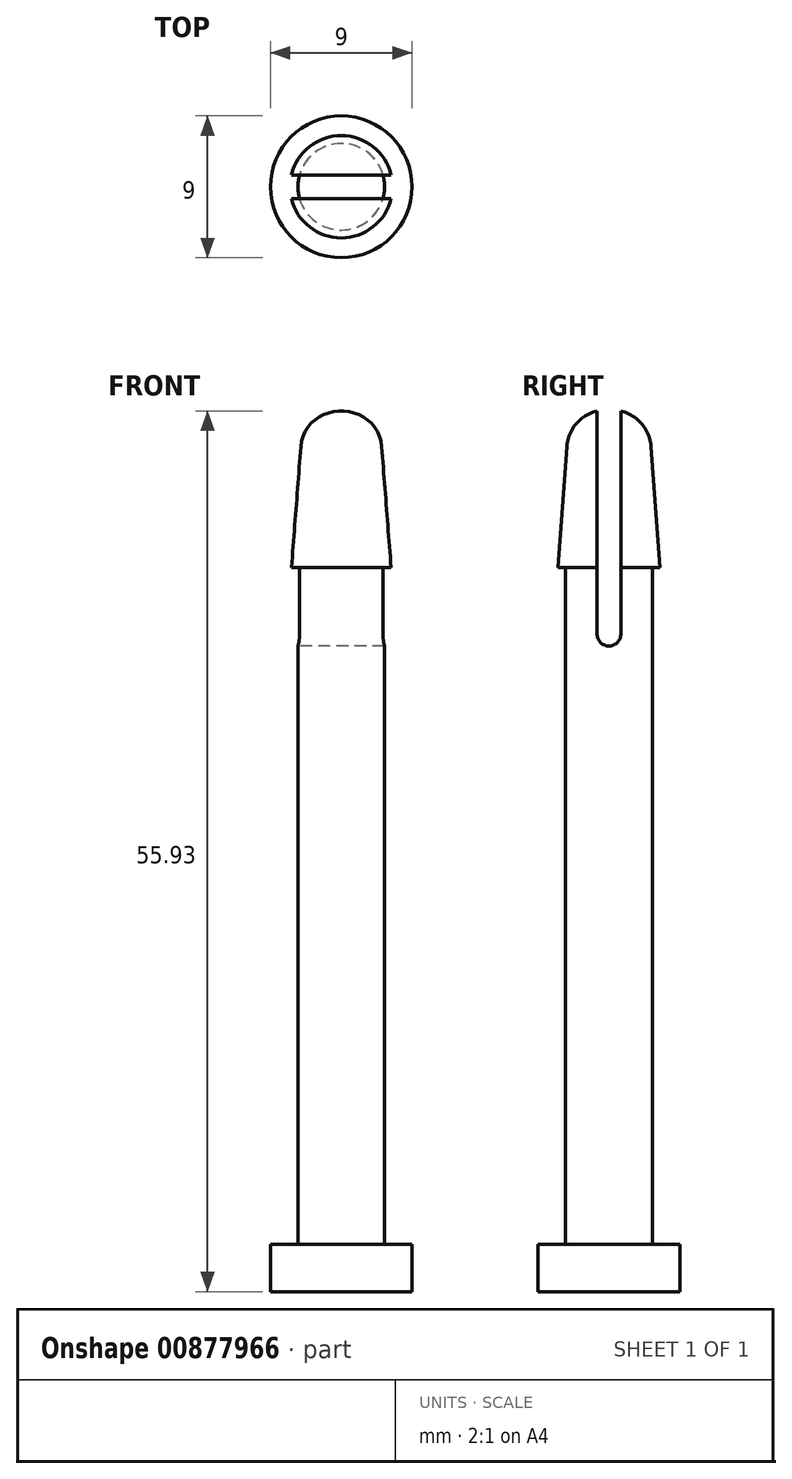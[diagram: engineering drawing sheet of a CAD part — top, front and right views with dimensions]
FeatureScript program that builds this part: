
annotation { "Feature Type Name" : "Feature", "Feature Type Description" : "" }
export const myFeature = defineFeature(function(context is Context, id is Id, definition is map)
    precondition{}
    {
        {
            var Q0;
            Q0=qCreatedBy(makeId("Top.planeOp"),FACE);
            var sketch = newSketch(context, id + "F0", { "sketchPlane" : qUnion([Q0])});
            skCircle(sketch, "E0", {"center": v(0, 0) * mm, "radius": 4.5 * mm});
            skSolve(sketch);
        }
        {
            var Q0;
            Q0 = qSketchRegion(id + "F0", true);
            extrude(context, id + "F1", {"entities" : qUnion([Q0]), "depth" : 3 * mm, "offsetDistance" : 25 * mm});
        }
        {
            var Q0;
            Q0=makeQuery(id+"F1.opExtrude","CAP_FACE",FACE,{"disambiguationData":[OSD([sQuery(id+"F0.wireOp",EDGE,"E0")])],"isStart":false});
            var sketch = newSketch(context, id + "F2", { "sketchPlane" : qUnion([Q0])});
            skCircle(sketch, "E1", {"center": v(0, 0) * mm, "radius": 2.75 * mm});
            skSolve(sketch);
        }
        {
            var Q0;
            Q0 = qSketchRegion(id + "F2", true);
            extrude(context, id + "F3", {"entities" : qUnion([Q0]), "operationType" : NewBodyOperationType.ADD, "depth" : 43 * mm, "offsetDistance" : 25 * mm});
        }
        {
            var Q0;
            Q0=qCreatedBy(makeId("Front.planeOp"),FACE);
            var sketch = newSketch(context, id + "F4", { "sketchPlane" : qUnion([Q0])});
            skLineSegment(sketch, "E2", {"start": v(0, 46) * mm, "end": v(3.25, 46) * mm});
            skLineSegment(sketch, "E3", {"start": v(3.25, 46) * mm, "end": v(2.5, 56) * mm});
            skLineSegment(sketch, "E4", {"start": v(2.5, 56) * mm, "end": v(0, 56) * mm});
            skLineSegment(sketch, "E5", {"start": v(0, 56) * mm, "end": v(0, 46) * mm});
            skSolve(sketch);
        }
        {
            var Q0;
            Q0 = qSketchRegion(id + "F4", true);
            var Q1;
            Q1=sQuery(id+"F4.wireOp",EDGE,"E5");
            revolve(context, id + "F5", {"operationType" : NewBodyOperationType.ADD, "surfaceOperationType" : NewSurfaceOperationType.NEW, "entities" : qUnion([Q0]), "axis" : qUnion([Q1]), "revolveType" : RevolveType.FULL});
        }
        {
            var Q0;
            Q0=makeQuery(id+"F5.opRevolve","SWEPT_FACE",FACE,{"disambiguationData":[OSD([sQuery(id+"F4.wireOp",EDGE,"E4")])]});
            var sketch = newSketch(context, id + "F6", { "sketchPlane" : qUnion([Q0])});
            skLineSegment(sketch, "E6.bottom", {"start": v(-5, 0.75) * mm, "end": v(5, 0.75) * mm});
            skLineSegment(sketch, "E6.top", {"start": v(-5, -0.75) * mm, "end": v(5, -0.75) * mm});
            skLineSegment(sketch, "E6.left", {"start": v(-5, 0.75) * mm, "end": v(-5, -0.75) * mm});
            skLineSegment(sketch, "E6.right", {"start": v(5, 0.75) * mm, "end": v(5, -0.75) * mm});
            skLineSegment(sketch, "E7", {"start": v(-5, -0.75) * mm, "end": v(5, 0.75) * mm, "construction": true});
            skLineSegment(sketch, "E8", {"start": v(5, -0.75) * mm, "end": v(-5, 0.75) * mm, "construction": true});
            skPoint(sketch, "E9.positionSnap0", {"position": v(0, 0) * mm});
            skSolve(sketch);
        }
        {
            var Q0;
            Q0 = qSketchRegion(id + "F6", true);
            extrude(context, id + "F7", {"entities" : qUnion([Q0]), "operationType" : NewBodyOperationType.REMOVE, "oppositeDirection" : true, "depth" : 15 * mm, "offsetDistance" : 25 * mm});
        }
        {
            var Q0;
            {var subQ0=sQuery(id+"F4.wireOp",EDGE,"E3");var subQ1=sQuery(id+"F4.wireOp",EDGE,"E4");Q0=makeQuery(id+"F7.boolean.opBoolean","SPLIT",EDGE,{"disambiguationData":[TD([makeQuery(id+"F7.opExtrude","SWEPT_FACE",FACE,{"disambiguationData":[OSD([sQuery(id+"F6.wireOp",EDGE,"E6.bottom")])]})])],"derivedFrom":makeQuery(id+"F5.opRevolve","SWEPT_EDGE",EDGE,{"disambiguationData":[OSD([subQ0,subQ1])]})});}
            var Q1;
            {var subQ0=sQuery(id+"F4.wireOp",EDGE,"E3");var subQ1=sQuery(id+"F4.wireOp",EDGE,"E4");Q1=makeQuery(id+"F7.boolean.opBoolean","SPLIT",EDGE,{"disambiguationData":[TD([makeQuery(id+"F7.opExtrude","SWEPT_FACE",FACE,{"disambiguationData":[OSD([sQuery(id+"F6.wireOp",EDGE,"E6.top")])]})])],"derivedFrom":makeQuery(id+"F5.opRevolve","SWEPT_EDGE",EDGE,{"disambiguationData":[OSD([subQ0,subQ1])]})});}
            fillet(context, id + "F8", {"entities" : qUnion([Q0, Q1]), "radius" : 2.5 * mm, "tangentPropagation" : true, "allowEdgeOverflow" : false});
        }
        {
            var Q0;
            Q0=makeQuery(id+"F7.boolean.opBoolean","COPY",EDGE,{"derivedFrom":makeQuery(id+"F7.opExtrude","CAP_EDGE",EDGE,{"disambiguationData":[OSD([sQuery(id+"F6.wireOp",EDGE,"E6.bottom")])],"isStart":false})});
            var Q1;
            Q1=makeQuery(id+"F7.boolean.opBoolean","COPY",EDGE,{"derivedFrom":makeQuery(id+"F7.opExtrude","CAP_EDGE",EDGE,{"disambiguationData":[OSD([sQuery(id+"F6.wireOp",EDGE,"E6.top")])],"isStart":false})});
            fillet(context, id + "F9", {"entities" : qUnion([Q0, Q1]), "radius" : .75 * mm, "tangentPropagation" : true, "allowEdgeOverflow" : false});
        }
    });
